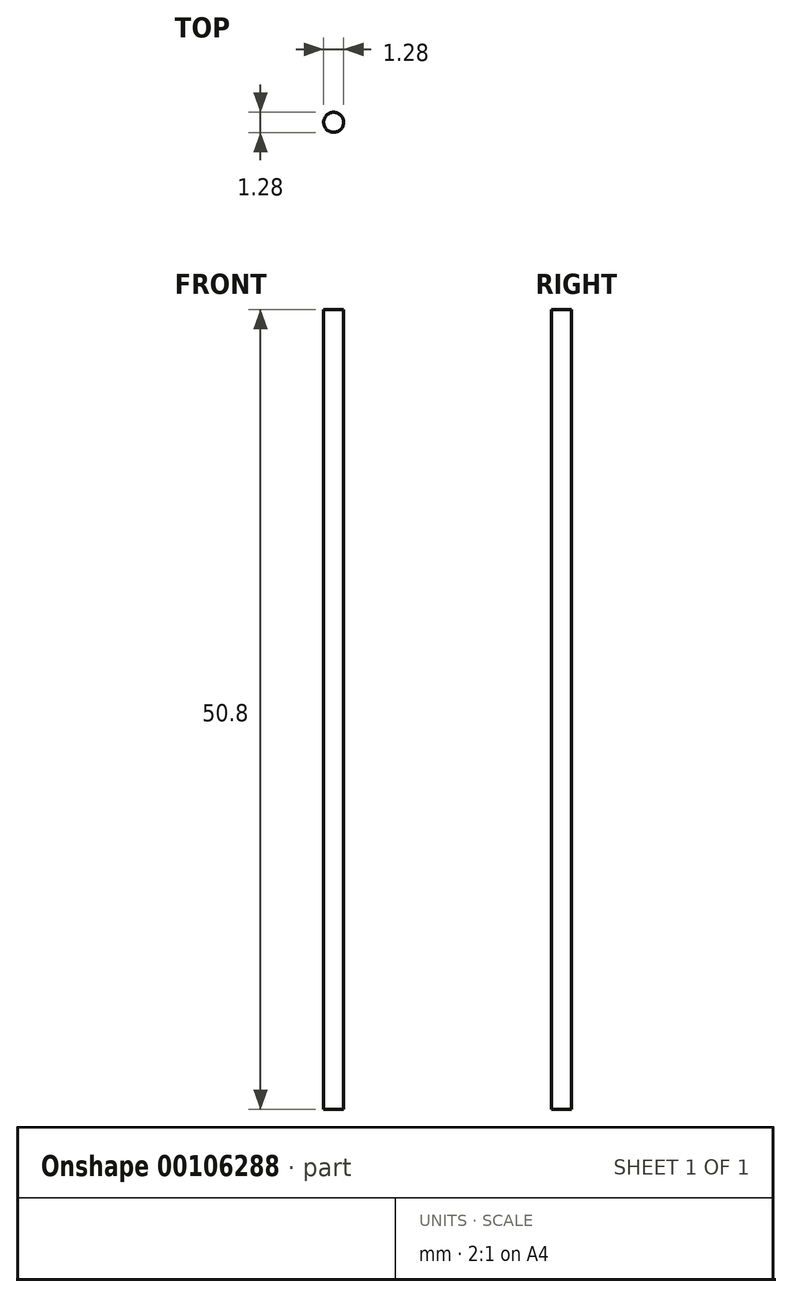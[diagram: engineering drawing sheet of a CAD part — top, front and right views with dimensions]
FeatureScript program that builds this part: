
annotation { "Feature Type Name" : "Feature", "Feature Type Description" : "" }
export const myFeature = defineFeature(function(context is Context, id is Id, definition is map)
    precondition{}
    {
        {
            var Q0;
            Q0=qCreatedBy(makeId("Top.planeOp"),FACE);
            var sketch = newSketch(context, id + "F0", { "sketchPlane" : qUnion([Q0])});
            skCircle(sketch, "E0", {"center": v(0, 0) * mm, "radius": 0.64 * mm});
            skSolve(sketch);
        }
        {
            var Q0;
            Q0 = qSketchRegion(id + "F0", true);
            extrude(context, id + "F1", {"entities" : qUnion([Q0]), "depth" : 50.8 * mm});
        }
    });
